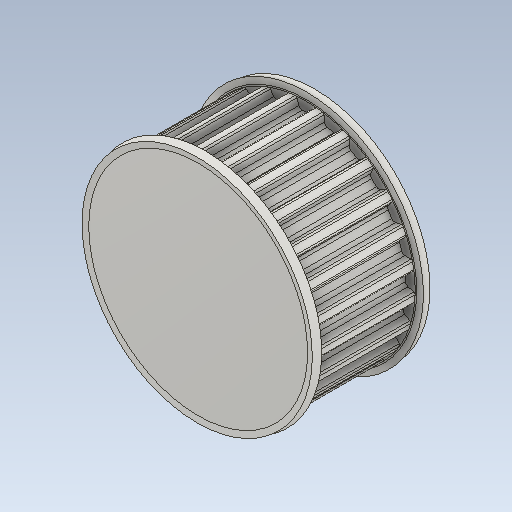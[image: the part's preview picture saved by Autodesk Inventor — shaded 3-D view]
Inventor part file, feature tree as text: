
AUTODESK INVENTOR PART (.ipt)
format: ipt  version: 2020 (Build 240168000, 168)  size: 461,312 bytes
history: native  units: mm (DEFAULTED — no unit token found)
features: other x3, extrude x2, fillet x1, pattern_circular x1
ambient origin geometry x8: Origin, YZ Plane, XZ Plane, XY Plane, X Axis, Y Axis, Z Axis, Center Point
bodies: Solid1 (feature_tree)
feature tree (7):
  other  "Pulley Sketch"
  extrude  "Base Body"  Depth=16.170142mm
  extrude  "Tooth"  Depth=0.254mm
  fillet  "Tooth Fillet"  Radius=0.6858mm
  pattern_circular  "Teeth"  [2 undecoded]
  other  "Left flange"
  other  "Right flange"
note: 2 required parameter values undecoded (feature->parameter linkage not recoverable at this tier; creation-order binding heuristic only, values carry confidence <= 0.55)
